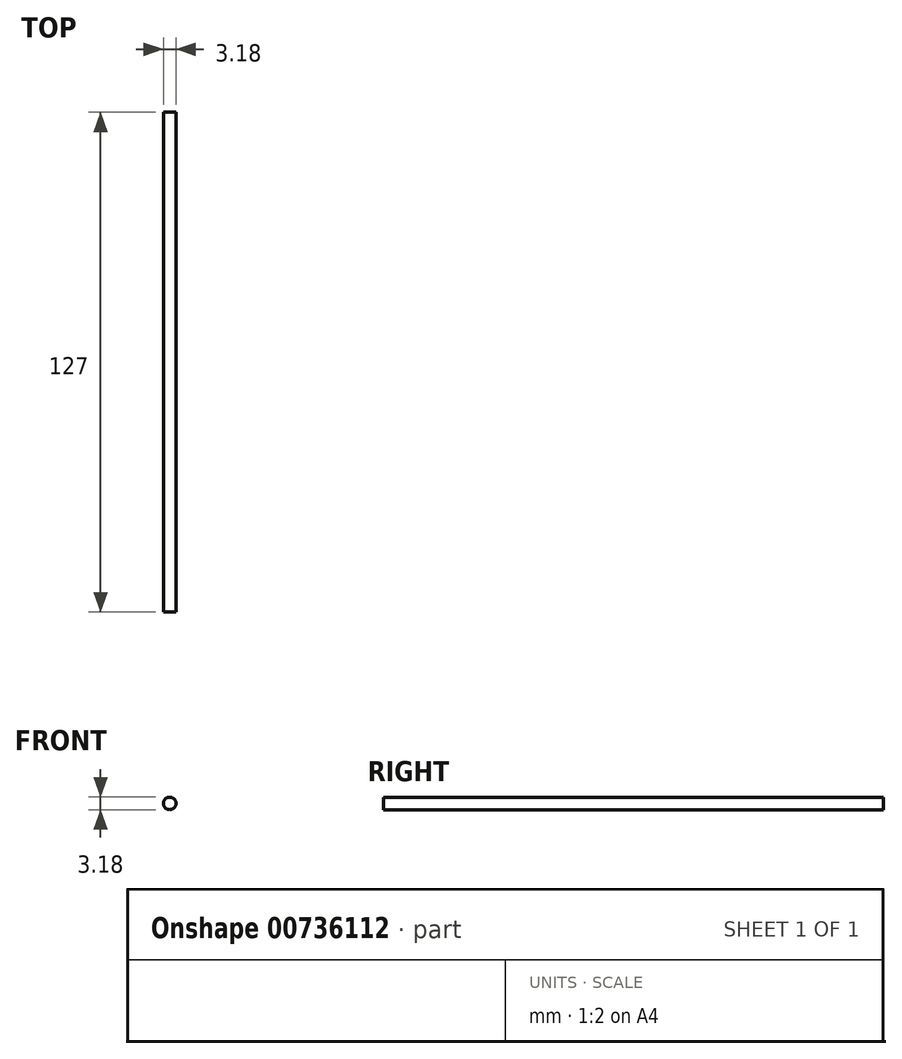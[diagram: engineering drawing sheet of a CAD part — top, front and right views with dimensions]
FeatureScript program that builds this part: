
annotation { "Feature Type Name" : "Feature", "Feature Type Description" : "" }
export const myFeature = defineFeature(function(context is Context, id is Id, definition is map)
    precondition{}
    {
        {
            var Q0;
            Q0=qCreatedBy(makeId("Front.planeOp"),FACE);
            var sketch = newSketch(context, id + "F0", { "sketchPlane" : qUnion([Q0])});
            skCircle(sketch, "E0", {"center": v(0, 0) * mm, "radius": 1.59 * mm});
            skSolve(sketch);
        }
        {
            var Q0;
            Q0 = qSketchRegion(id + "F0", true);
            extrude(context, id + "F1", {"entities" : qUnion([Q0]), "oppositeDirection" : true, "depth" : 127 * mm, "offsetDistance" : 25.4 * mm});
        }
    });
